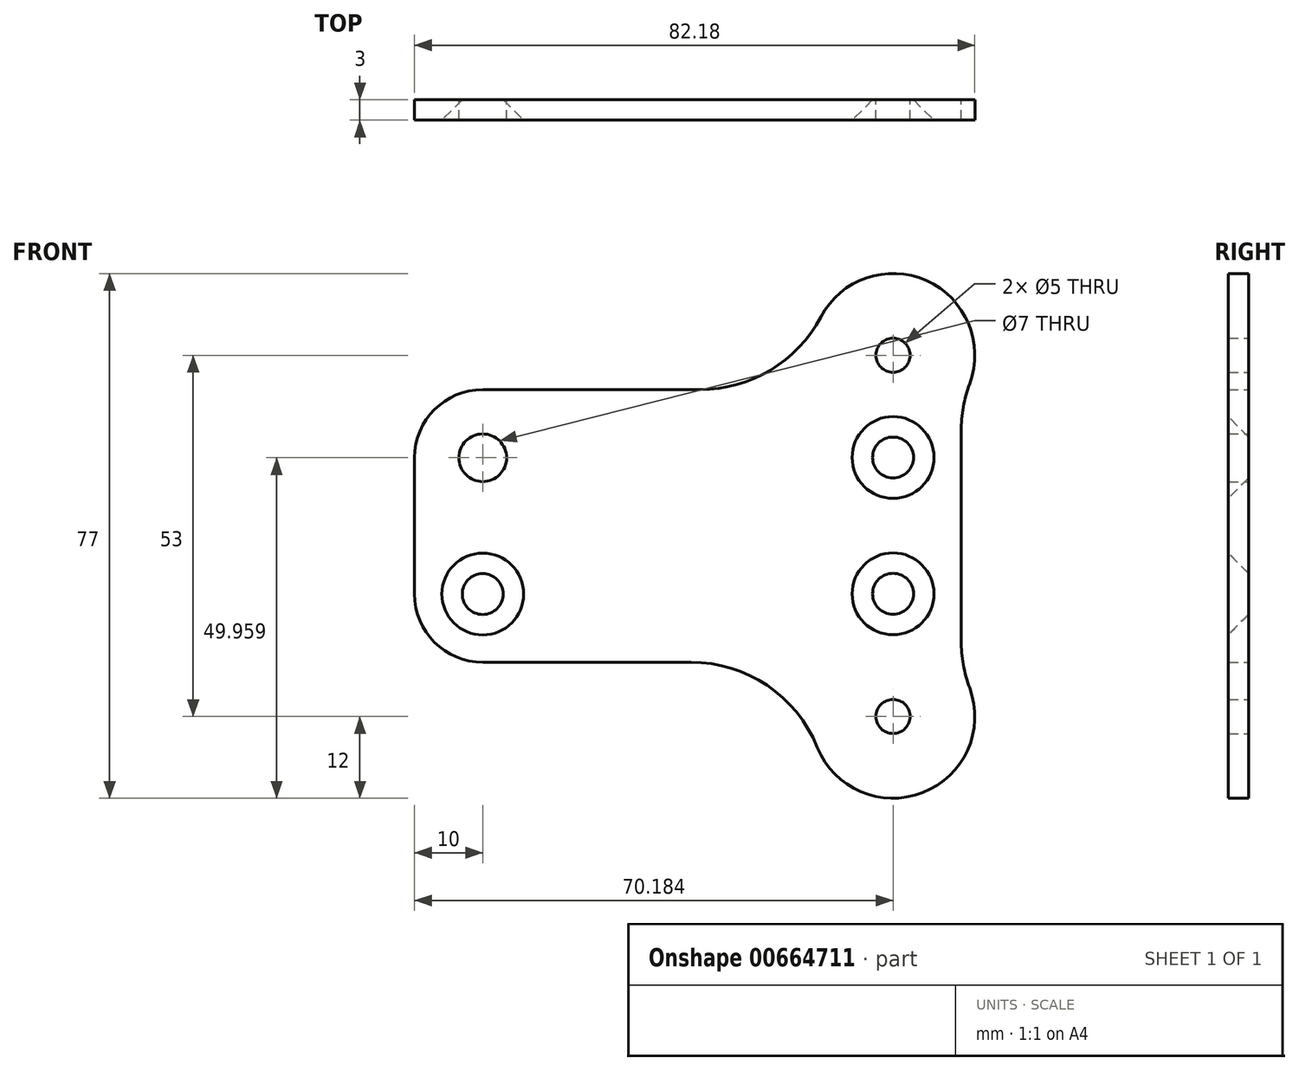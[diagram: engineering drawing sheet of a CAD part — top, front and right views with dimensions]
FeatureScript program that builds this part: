
annotation { "Feature Type Name" : "Feature", "Feature Type Description" : "" }
export const myFeature = defineFeature(function(context is Context, id is Id, definition is map)
    precondition{}
    {
        {
            var Q0;
            Q0=qCreatedBy(makeId("Front.planeOp"),FACE);
            var sketch = newSketch(context, id + "F0", { "sketchPlane" : qUnion([Q0])});
            skPoint(sketch, "E0.middle", {"position": v(0, 0) * mm});
            skLineSegment(sketch, "E1.0", {"start": v(30.18, 10) * mm, "end": v(30.18, 10) * mm});
            skLineSegment(sketch, "E2.0", {"start": v(30.18, -10) * mm, "end": v(-50, -10.05) * mm, "construction": true});
            skLineSegment(sketch, "E3.0", {"start": v(50, 25) * mm, "end": v(-50, 25) * mm, "construction": true});
            skLineSegment(sketch, "E4.0", {"start": v(30.18, 49.26) * mm, "end": v(30.18, -50.74) * mm, "construction": true});
            skCircle(sketch, "E5", {"center": v(30.18, 25) * mm, "radius": 2.5 * mm});
            skCircle(sketch, "E6", {"center": v(-30, -10.04) * mm, "radius": 2.5 * mm});
            skCircle(sketch, "E7", {"center": v(-30, 9.96) * mm, "radius": 3.5 * mm});
            skCircle(sketch, "E8", {"center": v(30.18, 10) * mm, "radius": 2.5 * mm});
            skCircle(sketch, "E9", {"center": v(30.18, -10) * mm, "radius": 2.5 * mm});
            skLineSegment(sketch, "E10", {"start": v(-40, 34) * mm, "end": v(42.18, 34) * mm, "construction": true});
            skLineSegment(sketch, "E11", {"start": v(-40, -40) * mm, "end": v(42.18, -40) * mm, "construction": true});
            skLineSegment(sketch, "E12", {"start": v(42.18, 34) * mm, "end": v(42.18, -40) * mm, "construction": true});
            skLineSegment(sketch, "E13.0", {"start": v(50, -28) * mm, "end": v(-50, -28) * mm, "construction": true});
            skCircle(sketch, "E14", {"center": v(30.18, -28) * mm, "radius": 2.5 * mm});
            skLineSegment(sketch, "E15", {"start": v(40.18, 13.86) * mm, "end": v(40.18, -16.86) * mm});
            skArc(sketch, "E16", {"start": v(41.43, 20.82) * mm, "mid": v(35.09, 35.95) * mm, "end": v(19.58, 30.6) * mm});
            skArc(sketch, "E17", {"start": v(19.07, -32.52) * mm, "mid": v(34.53, -39.19) * mm, "end": v(41.43, -23.82) * mm});
            skLineSegment(sketch, "E18", {"start": v(-30, 9.96) * mm, "end": v(-30, -10.04) * mm});
            skLineSegment(sketch, "E19", {"start": v(-30, -0.04) * mm, "end": v(18.22, -0.04) * mm});
            skLineSegment(sketch, "E20.0", {"start": v(-30, -20.04) * mm, "end": v(0.54, -20.04) * mm});
            skLineSegment(sketch, "E21.0", {"start": v(-30, 19.96) * mm, "end": v(1.9, 19.96) * mm});
            skLineSegment(sketch, "E22", {"start": v(-30, -20.04) * mm, "end": v(-30, -20.04) * mm});
            skLineSegment(sketch, "E23", {"start": v(-40, 9.96) * mm, "end": v(-40, -10.04) * mm});
            skPoint(sketch, "E24.visualSharp", {"position": v(-40, 19.96) * mm});
            skArc(sketch, "E24.filletArc", {"start": v(-30, 19.96) * mm, "mid": v(-37.07, 17.03) * mm, "end": v(-40, 9.96) * mm});
            skPoint(sketch, "E25.visualSharp", {"position": v(-40, -20.04) * mm});
            skArc(sketch, "E25.filletArc", {"start": v(-40, -10.04) * mm, "mid": v(-37.07, -17.11) * mm, "end": v(-30, -20.04) * mm});
            skPoint(sketch, "E26.visualSharp", {"position": v(19.3, 19.96) * mm});
            skArc(sketch, "E26.filletArc", {"start": v(1.9, 19.96) * mm, "mid": v(12.22, 22.83) * mm, "end": v(19.58, 30.6) * mm});
            skPoint(sketch, "E27.visualSharp", {"position": v(21.2, -20.04) * mm});
            skArc(sketch, "E27.filletArc", {"start": v(19.07, -32.52) * mm, "mid": v(11.7, -23.45) * mm, "end": v(0.54, -20.04) * mm});
            skArc(sketch, "E28.filletArc", {"start": v(40.18, -16.86) * mm, "mid": v(40.5, -20.4) * mm, "end": v(41.43, -23.82) * mm});
            skArc(sketch, "E29.filletArc", {"start": v(41.43, 20.82) * mm, "mid": v(40.5, 17.4) * mm, "end": v(40.18, 13.86) * mm});
            skSolve(sketch);
        }
        {
            var Q0;
            Q0=makeQuery(id+"F0.imprint","IMPRINT",FACE,{"disambiguationData":[TD([[makeQuery(id+"F0.imprint","IMPRINT",EDGE,{"derivedFrom":sQuery(id+"F0.wireOp",EDGE,"E5")}),-1.0]])]});
            extrude(context, id + "F1", {"entities" : qUnion([Q0]), "depth" : 3 * mm, "offsetDistance" : 25 * mm});
        }
        {
            var Q0;
            Q0=makeQuery(id+"F1.opExtrude","CAP_EDGE",EDGE,{"disambiguationData":[OSD([sQuery(id+"F0.wireOp",EDGE,"E6")])],"isStart":false});
            var Q1;
            Q1=makeQuery(id+"F1.opExtrude","CAP_EDGE",EDGE,{"disambiguationData":[OSD([sQuery(id+"F0.wireOp",EDGE,"E9")])],"isStart":false});
            var Q2;
            Q2=makeQuery(id+"F1.opExtrude","CAP_EDGE",EDGE,{"disambiguationData":[OSD([sQuery(id+"F0.wireOp",EDGE,"E8")])],"isStart":false});
            chamfer(context, id + "F2", {"entities" : qUnion([Q0, Q1, Q2]), "width" : 3.5 * mm, "tangentPropagation" : true});
        }
    });
